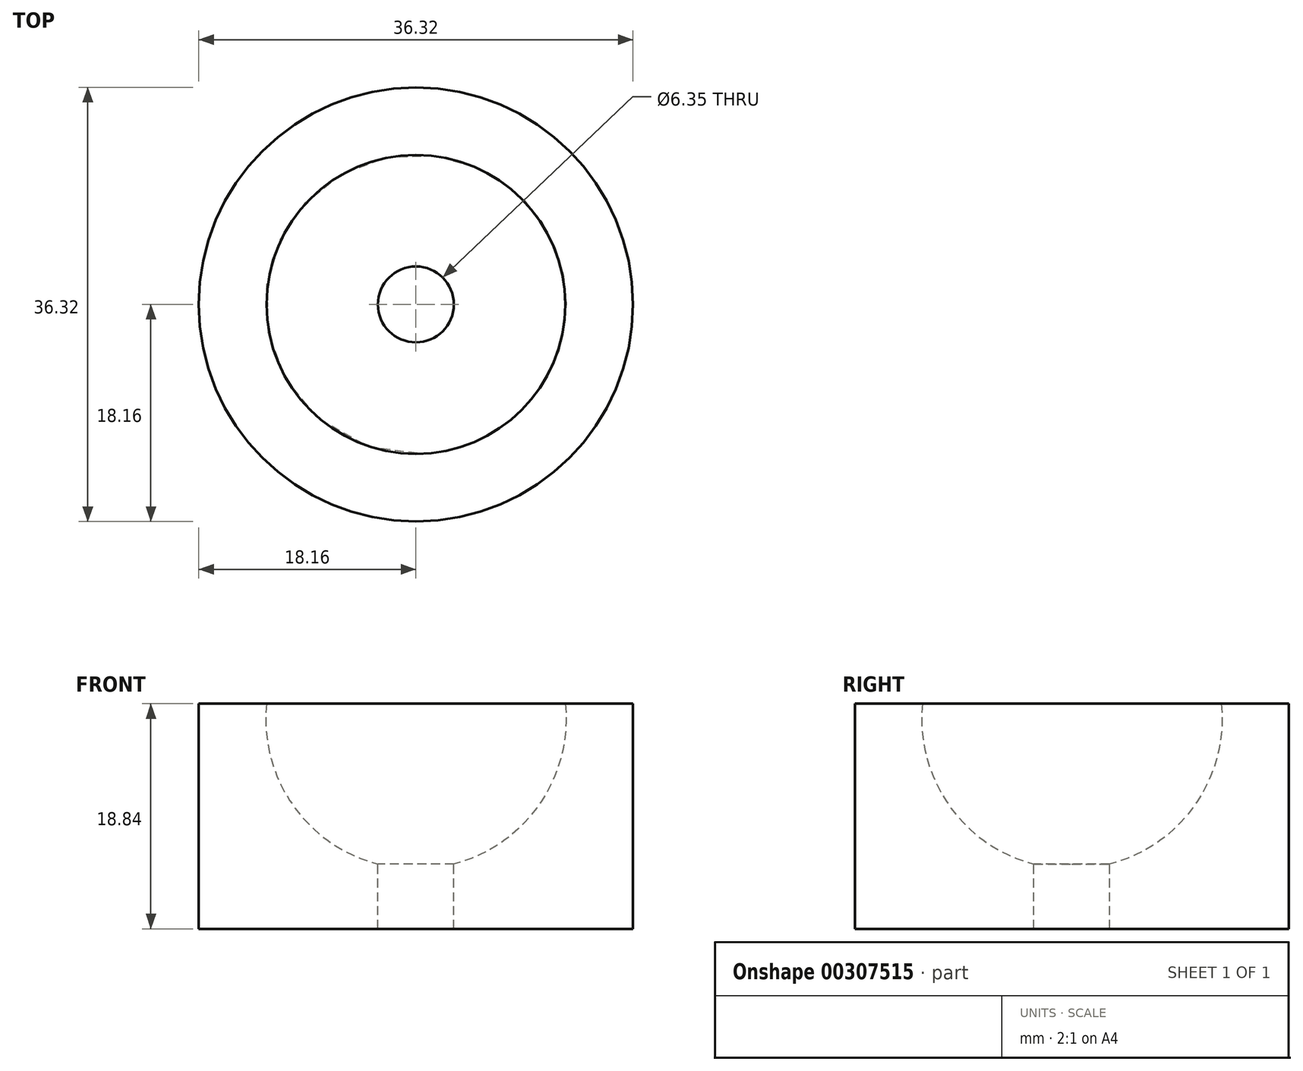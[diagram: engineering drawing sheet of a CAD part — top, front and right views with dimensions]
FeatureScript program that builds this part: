
annotation { "Feature Type Name" : "Feature", "Feature Type Description" : "" }
export const myFeature = defineFeature(function(context is Context, id is Id, definition is map)
    precondition{}
    {
        {
            var Q0;
            Q0=qCreatedBy(makeId("Front.planeOp"),FACE);
            var sketch = newSketch(context, id + "F0", { "sketchPlane" : qUnion([Q0])});
            skArc(sketch, "E0", {"start": v(-12.5, -0.86) * mm, "mid": v(-9.33, -10.56) * mm, "end": v(0, -14.7) * mm});
            skArc(sketch, "E1", {"start": v(0, -14.7) * mm, "mid": v(9.33, 6.29) * mm, "end": v(-12.5, -0.86) * mm, "construction": true});
            skLineSegment(sketch, "E2", {"start": v(-12.5, -0.86) * mm, "end": v(-18.16, -0.86) * mm});
            skLineSegment(sketch, "E3", {"start": v(-18.16, -0.86) * mm, "end": v(-18.16, -19.7) * mm});
            skLineSegment(sketch, "E4", {"start": v(-18.16, -19.7) * mm, "end": v(0, -19.7) * mm});
            skLineSegment(sketch, "E5", {"start": v(0, -14.7) * mm, "end": v(0, -19.7) * mm});
            skSolve(sketch);
        }
        {
            var Q0;
            Q0=makeQuery(id+"F0.imprint","IMPRINT",FACE,{"disambiguationData":[TD([[makeQuery(id+"F0.imprint","IMPRINT",EDGE,{"derivedFrom":sQuery(id+"F0.wireOp",EDGE,"E0")}),-1.0]])]});
            var Q1;
            Q1=qSketchRegion(id+"F2",true);
            var Q2;
            Q2=sQuery(id+"F0.wireOp",EDGE,"E5");
            revolve(context, id + "F1", {"entities" : qUnion([Q0, Q1]), "axis" : qUnion([Q2]), "revolveType" : RevolveType.FULL});
        }
        {
            var Q0;
            Q0=qCreatedBy(makeId("Top.planeOp"),FACE);
            var sketch = newSketch(context, id + "F2", { "sketchPlane" : qUnion([Q0])});
            skPoint(sketch, "E6", {"position": v(0, 0) * mm});
            skSolve(sketch);
        }
        {
            var Q0;
            Q0=sQuery(id+"F2.wireOp",VERTEX,"E6");
            var Q1;
            Q1=makeQuery(id+"F1.opRevolve","SWEPT_BODY",BODY,{"disambiguationData":[OSD([sQuery(id+"F0.wireOp",EDGE,"E0"),sQuery(id+"F0.wireOp",EDGE,"E2"),sQuery(id+"F0.wireOp",EDGE,"E3"),sQuery(id+"F0.wireOp",EDGE,"E4"),sQuery(id+"F0.wireOp",EDGE,"E5")])]});
            hole(context, id + "F3", {"style" : HoleStyle.C_SINK, "endStyle" : HoleEndStyle.THROUGH, "holeDiameter" : 6.35 * mm, "cSinkDiameter" : 6.5 * mm, "cSinkAngle" : 90 * degree, "startFromSketch" : true, "locations" : qUnion([Q0]), "scope" : qUnion([Q1]), "tappedDepth" : 12 * mm, "tapClearance" : 3});
        }
    });
